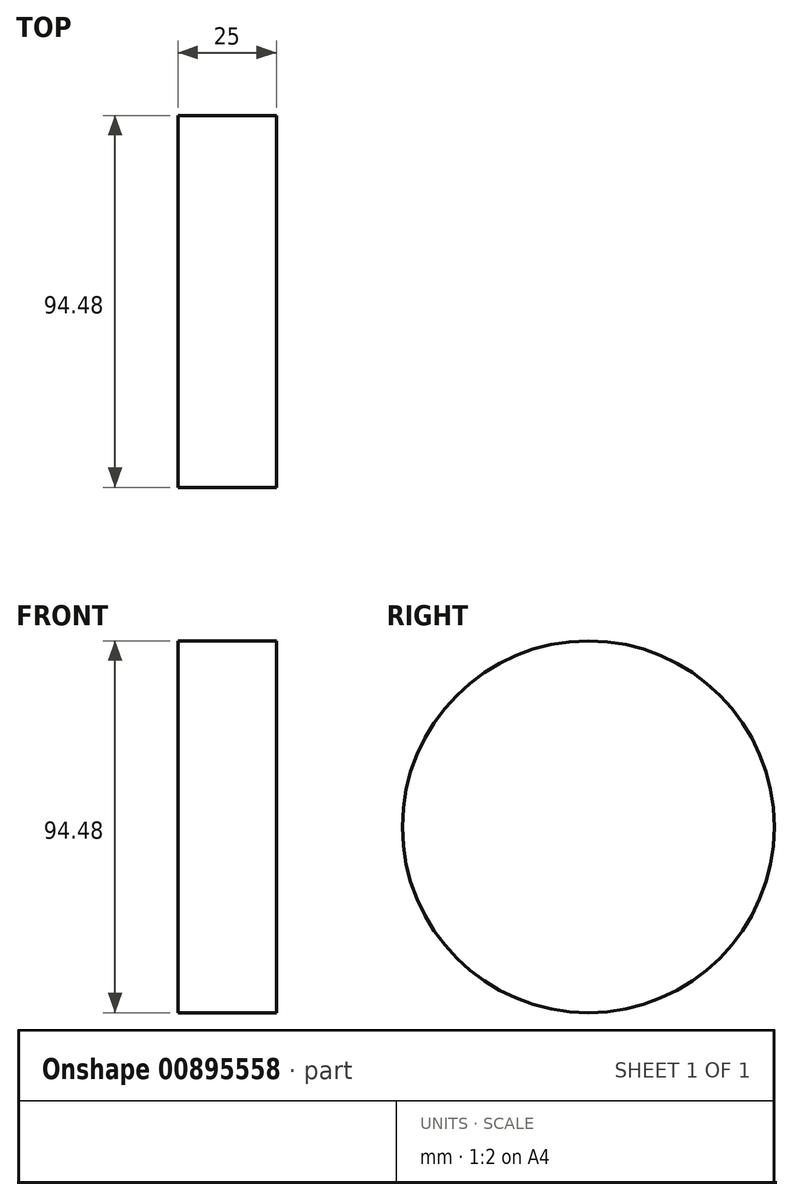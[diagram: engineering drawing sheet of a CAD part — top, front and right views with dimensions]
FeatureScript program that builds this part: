
annotation { "Feature Type Name" : "Feature", "Feature Type Description" : "" }
export const myFeature = defineFeature(function(context is Context, id is Id, definition is map)
    precondition{}
    {
        {
            var Q0;
            Q0=qCreatedBy(makeId("Right.planeOp"),FACE);
            var sketch = newSketch(context, id + "F0", { "sketchPlane" : qUnion([Q0])});
            skCircle(sketch, "E0", {"center": v(0, 0) * mm, "radius": 47.24 * mm});
            skSolve(sketch);
        }
        {
            var Q0;
            Q0=makeQuery(id+"F0.imprint","IMPRINT",FACE,{"disambiguationData":[TD([[makeQuery(id+"F0.imprint","IMPRINT",EDGE,{"derivedFrom":sQuery(id+"F0.wireOp",EDGE,"E0")}),1.0]])]});
            extrude(context, id + "F1", {"entities" : qUnion([Q0]), "depth" : 25 * mm, "offsetDistance" : 25 * mm});
        }
    });
